# Revit family: 0052362 Sylvania Lighting Fixture RANA LINEAR R 3KLM NW LOUV+PRI 1-10 WHIT EMERGENCY
name_source: partatom
category: Lighting Fixtures
revit_build: Autodesk Revit 2016 (Build: 20150220_1215(x64)
units: mm (PartAtom-declared; Revit-internal decimal feet)

## family parameters
Cut with Voids When Loaded = No
Host = Face
Light Source = Yes
OmniClass Number = 23.80.70.00
OmniClass Title = Lighting
Part Type = Normal
Room Calculation Point = No
Round Connector Dimension = Use Diameter
Shared = No

## types (2) — shared parameters
Apparent Load = 31 VA
Assembly Code = D5020200
AssetType = Fixed
ClassificationName = Uniclass2015
ClassificationValue = EF_70_80
Color Filter = 16777215
Default Elevation = 1219 mm
Description = Ceiling recessed LED Linear luminaire with Louvre + Micro Prismatic Optic, Dimensions: 1154mm x 90mm x 91mm, Direct, White Body,  1-10V Dimmable, Emergency 3 hours maintained,  Neutral White LED (4000K), 3160lm, 31W, 102lm/W efficacy, CRI>80, 3 SDCM (3-step MacAdam ellipse), Low LED Flicker (+/-5%), UGR<19, L90B10 at 50,000 hours,  Electric Class1, Glow Wire Test 850°C, Can be covered with building insulation of Glass wool type
Diffuser_SYL = No
Dimming Lamp Color Temperature Shift = <None>
DocumentationLiterature = http://www.sylvania-lighting.com
ElectricShockClassification = Class I
Emit Shape Visible in Rendering = No
Emit from Rectangle Length = 1130 mm  [stored 3.70735 ft]
Emit from Rectangle Width = 61 mm  [stored 0.200131 ft]
IfcExportAs = IfcLightFixtureType
IfcExportType = IfcLightFixtureType
ImpactProtectionIndex = IK07
IngressProtection = IP20
Inset_SYL = 12 mm  [stored 0.0393701 ft]
Keynote = 16500
Lamp = LED
LampColourRenderingIndex = 80
LampColourTemperature = 4000 K
LampsType = LED
Length_SYL = 1154 mm  [stored 3.78609 ft]
LightOutputRatio = 100
LouverNumber_SYL = 32
LouverPrizm_SYL = Yes
Manufacturer = Feilo Sylvania
ManufacturerName = Feilo Sylvania
Material = steel housing, polycarbonate diffuser
Material_1_SYL = Body-Sylvania-Rana-White
Material_2_SYL = Diffuser-Sylvania-Rana
Material_3_SYL = <By Category>
Material_4_SYL = <By Category>
Model = RANA LINEAR R 3KLM NW LOUV+PRI 1-10 WHIT EMERGENCY
ModelNumber = 0052362
ModelReference = RANA LINEAR R 3KLM NW LOUV+PRI 1-10 WHIT EMERGENCY
Name = RANA LINEAR R 3KLM NW LOUV+PRI 1-10 WHIT EMERGENCY
NominalDepth = 90 mm  [stored 0.295276 ft]
NominalHeight = 91 mm
NominalLength = 1150 mm
PowerConsumption = 31 W
RecessLength_SYL = 1142 mm  [stored 3.74672 ft]
RecessWidth_SYL = 72 mm  [stored 0.23622 ft]
ReflectorLength_SYL = 1130 mm  [stored 3.70735 ft]
Tilt Angle = -90.00°
Type Image = <None>
TypeName = RANA LINEAR R 3KLM NW LOUV+PRI 1-10 WHIT EMERGENCY
URL = http://www.sylvania-lighting.com
Voltage = 0 V
Weight = 3.75 kg
Width_SYL = 90 mm  [stored 0.295276 ft]
zero-valued in all types: Cost, PowerFactor

## per-type parameters (varying)
| type | LampNominalLuminous | LuminousEfficacy | Photometric Web File |
| 0052362 RANA LINEAR R 3KLM NW LOUV+PRI 1-10 EM | 3160 lm | 101.9 lm/W | 0052362.ies |
| 0052362 RANA LINEAR R 3KLM NW LOUV+PRI 1-10 EM Emergency mode | 551 lm | 17.796 lm/W | 0052362EM.ies |

note: [stored X ft] marks values corroborated as IEEE doubles in the binary element streams (Revit-internal decimal feet)

## geometry (parser evidence)
native form markers: Sweep x9
no freeform markers — native parametric forms only
